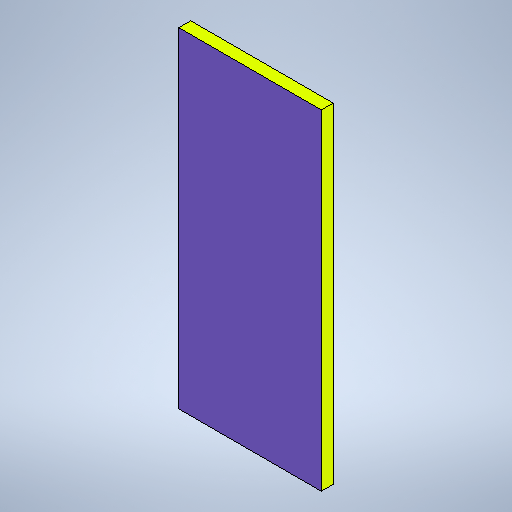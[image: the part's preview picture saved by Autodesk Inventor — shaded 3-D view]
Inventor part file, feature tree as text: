
AUTODESK INVENTOR PART (.ipt)
format: ipt  version: 2025.3 (Build 293356000, 356)  size: 224,768 bytes
history: native  units: mm
features: extrude x1, chamfer x1
ambient origin geometry x8: Origin, YZ Plane, XZ Plane, XY Plane, X Axis, Y Axis, Z Axis, Center Point
bodies: Solid1 (feature_tree)
feature tree (2):
  extrude  "Extrusion1"  Depth=1200.0mm
  chamfer  "Chamfer1"  Distance=2780.0mm
